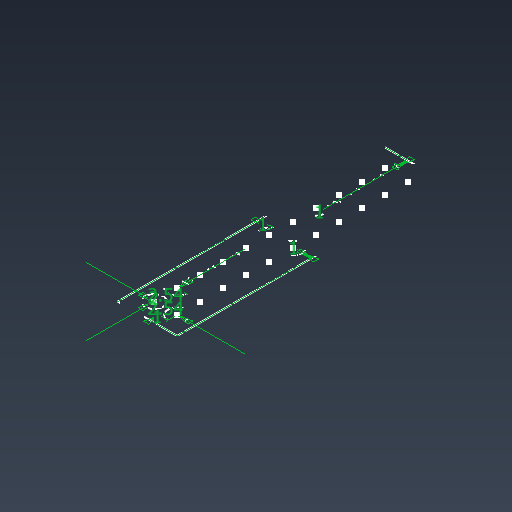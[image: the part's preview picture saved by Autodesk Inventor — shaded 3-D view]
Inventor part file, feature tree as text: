
AUTODESK INVENTOR PART (.ipt)
format: ipt  version: 2025.3 (Build 293356000, 356)  size: 86,016 bytes
history: native  units: mm
features: sketch x2
ambient origin geometry x8: Origin, YZ Plane, XZ Plane, XY Plane, X Axis, Y Axis, Z Axis, Center Point
feature tree (2):
  sketch  "Sketch1"  dims[d0=2.0mm]
  sketch  "Sketch Rectangular Pattern1"  dims[d1=20.0mm d3=2.54mm d4=110.0mm d6=2.54mm d9=1.0mm d10=1.0mm d11=1.0mm d12=1.0mm]
